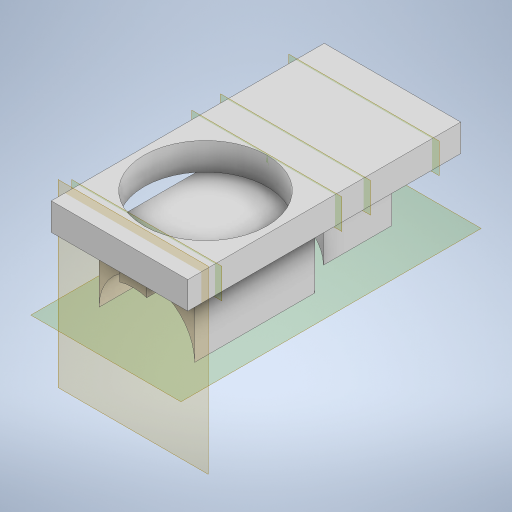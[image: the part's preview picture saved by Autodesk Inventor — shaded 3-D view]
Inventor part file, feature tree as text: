
AUTODESK INVENTOR PART (.ipt)
format: ipt  version: 2023 (Build 270158000, 158)  size: 325,632 bytes
history: native  units: in
note: dims shown in document units (in); Inventor stores cm internally (conversion verified against a paired STEP export)
features: extrude x6, plane x6, sketch x4, projected_geometry x3
ambient origin geometry x8: Origin, YZ Plane, XZ Plane, XY Plane, X Axis, Y Axis, Z Axis, Center Point
bodies: Solid1 (feature_tree)
feature tree (19):
  sketch  "Sketch1"  dims[d0=1.9685in d1=3.937in d2=1.7323in d3=90.0deg d4=1.378in d5=0.3937in d6=0.9882in d7=90.0deg d8=0.8071in d9=0.1969in d10=90.0deg d11=0.0in d12=0.3937in d13=0.0in]
  extrude  "Extrusion1"  Depth=0.3937in TaperAngle=0.0deg
  plane  "Work Plane1"
  plane  "Work Plane2"
  plane  "Work Plane3"
  plane  "Work Plane4"
  sketch  "Sketch2"  dims[d14=1.9685in d15=1.9685in]
  sketch  "Sketch3"  dims[d16=0.8071in d17=1.9685in]
  sketch  "Sketch4"  dims[d18=1.9685in d19=1.378in d20=1.9685in d21=1.9685in d22=0.3937in d23=0.3937in d24=0.1969in d25=0.3937in d26=0.3937in d27=0.0in d28=0.3937in d29=0.0in d30=0.3937in d31=0.0in d32=0.3937in d33=0.0in d34=0.3937in d35=0.0in d36=1.7717in]
  plane  "Work Plane5"
  extrude  "Extrusion2"  Depth=1.9685in
  extrude  "Extrusion3"  Depth=1.9685in
  plane  "Work Plane6"
  extrude  "Extrusion4"  Depth=1.378in
  extrude  "Extrusion5"  Depth=1.9685in
  extrude  "Extrusion6"  Depth=1.9685in
  projected_geometry  "Projected Loop1"
  projected_geometry  "Projected Loop2"
  projected_geometry  "Projected Loop3"
